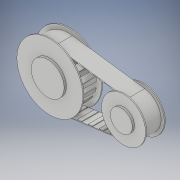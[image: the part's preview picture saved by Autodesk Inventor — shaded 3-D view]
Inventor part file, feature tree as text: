
AUTODESK INVENTOR PART (.ipt)
format: ipt  version: 2018 (Build 220112000, 112)  size: 402,944 bytes
history: native  units: in
note: dims shown in document units (in); Inventor stores cm internally (conversion verified against a paired STEP export)
features: sketch x10, extrude x8, pattern_linear x3, plane x2, pattern_circular x2
ambient origin geometry x8: Origin, YZ Plane, XZ Plane, XY Plane, X Axis, Y Axis, Z Axis, Center Point
bodies: Solid1 (feature_tree), Solid3 (feature_tree)
feature tree (25):
  extrude  "Extrusion1"  Depth=3.937in
  plane  "Work Plane1"
  sketch  "Sketch2"  dims[d2=6.5945in d3=0.0984in d4=0.0in]
  plane  "Work Plane2"
  extrude  "Extrusion2"  Depth=0.0984in TaperAngle=0.0deg
  extrude  "Extrusion4"  Depth=0.0984in TaperAngle=0.0deg
  extrude  "Extrusion5"  Depth=1.5748in TaperAngle=0.0deg
  pattern_circular  "Circular Pattern1"  Count=8  [1 undecoded]
  pattern_circular  "Circular Pattern2"  Count=4  [1 undecoded]
  extrude  "Extrusion8"  Depth=0.0591in TaperAngle=360.0deg
  extrude  "Extrusion9"  Depth=0.0591in TaperAngle=360.0deg
  extrude  "Extrusion10"  Depth=1.5748in TaperAngle=0.0deg
  pattern_linear  "Rectangular Pattern1"  Count1=5  [1 undecoded]
  pattern_linear  "Rectangular Pattern2"  Spacing1=1.5094in  [1 undecoded]
  sketch  "Sketch11"  dims[d36=0.1969in d37=0.0in]
  extrude  "Extrusion11"  Depth=1.9685in
  pattern_linear  "Rectangular Pattern3"  Spacing1=0.3937in  [1 undecoded]
  sketch  "Sketch1"  dims[d0=5.9055in d1=3.937in]
  sketch  "Sketch3"  dims[d5=1.5748in d6=0.0984in d7=0.0in]
  sketch  "Sketch5"  dims[d12=4.9213in d13=1.5748in d14=0.0in d15=3.1496in d16=1.5748in d17=0.0in]
  sketch  "Sketch6"  dims[d20=0.0591in d22=7.0866in d23=360.0deg]
  sketch  "Sketch8"  dims[d25=0.0591in d26=4.7244in d27=360.0deg]
  sketch  "Sketch9"  dims[d29=0.0591in d32=1.5748in d33=0.0in]
  sketch  "Sketch10"  dims[d34=2.9528in d35=1.9685in]
  sketch  "Sketch12"  dims[d38=0.0591in d39=0.0591in d40=1.5094in d41=0.0in d42=1.9685in d44=0.9843in d45=0.3937in d46=0.7874in d48=0.9843in d49=1.5748in d50=0.0in d51=1.9685in d53=0.9843in d54=0.3937in d55=0.0591in]
note: 5 required parameter values undecoded (feature->parameter linkage not recoverable at this tier; creation-order binding heuristic only, values carry confidence <= 0.55)
